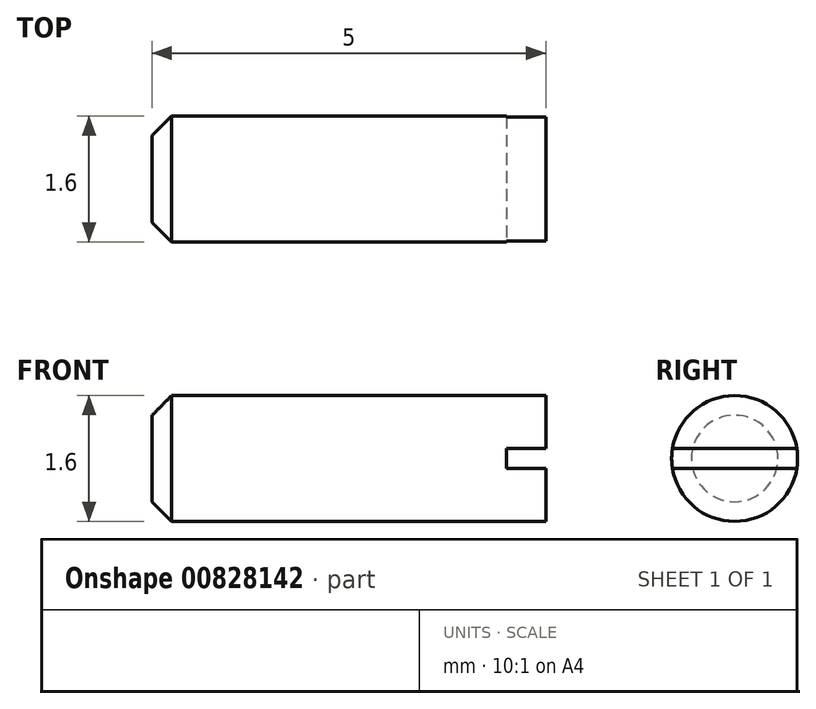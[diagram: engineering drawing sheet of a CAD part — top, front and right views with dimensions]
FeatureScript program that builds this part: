
annotation { "Feature Type Name" : "Feature", "Feature Type Description" : "" }
export const myFeature = defineFeature(function(context is Context, id is Id, definition is map)
    precondition{}
    {
        {
            var Q0;
            Q0=qCreatedBy(makeId("Front.planeOp"),FACE);
            var sketch = newSketch(context, id + "F0", { "sketchPlane" : qUnion([Q0])});
            skLineSegment(sketch, "E0.bottom", {"start": v(0, 0) * mm, "end": v(5, 0) * mm});
            skLineSegment(sketch, "E0.top", {"start": v(0, 0.8) * mm, "end": v(5, 0.8) * mm});
            skLineSegment(sketch, "E0.left", {"start": v(0, 0) * mm, "end": v(0, 0.8) * mm});
            skLineSegment(sketch, "E0.right", {"start": v(5, 0) * mm, "end": v(5, 0.8) * mm});
            skSolve(sketch);
        }
        {
            var Q0;
            Q0 = qSketchRegion(id + "F0", true);
            var Q1;
            Q1=sQuery(id+"F0.wireOp",EDGE,"E0.bottom");
            revolve(context, id + "F1", {"surfaceOperationType" : NewSurfaceOperationType.NEW, "entities" : qUnion([Q0]), "axis" : qUnion([Q1]), "revolveType" : RevolveType.FULL});
        }
        {
            var Q0;
            Q0=qCreatedBy(makeId("Front.planeOp"),FACE);
            var sketch = newSketch(context, id + "F2", { "sketchPlane" : qUnion([Q0])});
            skLineSegment(sketch, "E1.bottom", {"start": v(4.5, 0.12) * mm, "end": v(5, 0.12) * mm});
            skLineSegment(sketch, "E1.top", {"start": v(4.5, -0.12) * mm, "end": v(5, -0.12) * mm});
            skLineSegment(sketch, "E1.left", {"start": v(4.5, 0.12) * mm, "end": v(4.5, -0.12) * mm});
            skLineSegment(sketch, "E1.right", {"start": v(5, 0.12) * mm, "end": v(5, -0.12) * mm});
            skSolve(sketch);
        }
        {
            var Q0;
            Q0 = qSketchRegion(id + "F2", true);
            extrude(context, id + "F3", {"entities" : qUnion([Q0]), "operationType" : NewBodyOperationType.REMOVE, "endBound" : BoundingType.SYMMETRIC, "oppositeDirection" : true, "depth" : 25 * mm, "offsetDistance" : 25 * mm});
        }
        {
            var Q0;
            Q0=makeQuery(id+"F1.opRevolve","SWEPT_EDGE",EDGE,{"disambiguationData":[OSD([sQuery(id+"F0.wireOp",EDGE,"E0.top"),sQuery(id+"F0.wireOp",EDGE,"E0.left")])]});
            chamfer(context, id + "F4", {"entities" : qUnion([Q0]), "width" : 0.25 * mm, "tangentPropagation" : true});
        }
    });
